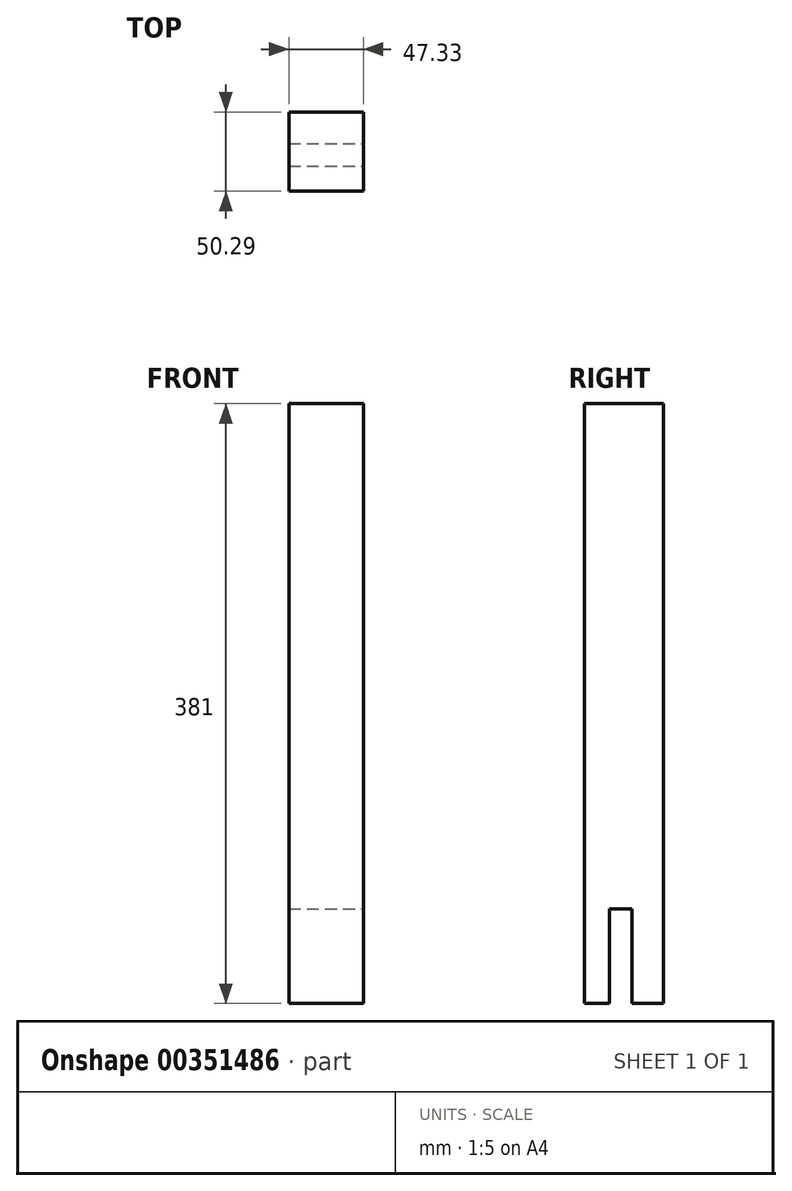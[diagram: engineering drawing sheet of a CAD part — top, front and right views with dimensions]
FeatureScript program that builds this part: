
annotation { "Feature Type Name" : "Feature", "Feature Type Description" : "" }
export const myFeature = defineFeature(function(context is Context, id is Id, definition is map)
    precondition{}
    {
        {
            var Q0;
            Q0=qCreatedBy(makeId("Top.planeOp"),FACE);
            var sketch = newSketch(context, id + "F0", { "sketchPlane" : qUnion([Q0])});
            skLineSegment(sketch, "E0", {"start": v(0, 50.29) * mm, "end": v(47.33, 50.29) * mm});
            skLineSegment(sketch, "E1", {"start": v(47.33, 50.29) * mm, "end": v(47.33, 0) * mm});
            skLineSegment(sketch, "E2", {"start": v(47.33, 0) * mm, "end": v(0, 0) * mm});
            skLineSegment(sketch, "E3", {"start": v(0, 0) * mm, "end": v(0, 50.29) * mm});
            skSolve(sketch);
        }
        {
            var Q0;
            Q0=makeQuery(id+"F0.imprint","IMPRINT",FACE,{"disambiguationData":[TD([[makeQuery(id+"F0.imprint","IMPRINT",EDGE,{"derivedFrom":sQuery(id+"F0.wireOp",EDGE,"E0")}),-1.0]])]});
            extrude(context, id + "F1", {"entities" : qUnion([Q0]), "depth" : 381 * mm});
        }
        {
            var Q0;
            Q0=makeQuery(id+"F1.opExtrude","SWEPT_FACE",FACE,{"disambiguationData":[OSD([sQuery(id+"F0.wireOp",EDGE,"E1")])]});
            var sketch = newSketch(context, id + "F2", { "sketchPlane" : qUnion([Q0])});
            skLineSegment(sketch, "E4.bottom", {"start": v(16.08, 0) * mm, "end": v(30.28, 0) * mm});
            skLineSegment(sketch, "E4.top", {"start": v(16.08, 60.04) * mm, "end": v(30.28, 60.04) * mm});
            skLineSegment(sketch, "E4.left", {"start": v(16.08, 0) * mm, "end": v(16.08, 60.04) * mm});
            skLineSegment(sketch, "E4.right", {"start": v(30.28, 0) * mm, "end": v(30.28, 60.04) * mm});
            skSolve(sketch);
        }
        {
            var Q0;
            Q0=makeQuery(id+"F2.imprint","IMPRINT",FACE,{"disambiguationData":[TD([[makeQuery(id+"F2.imprint","IMPRINT",EDGE,{"derivedFrom":sQuery(id+"F2.wireOp",EDGE,"E4.bottom")}),-1.0]])]});
            var Q1;
            Q1=makeQuery(id+"F1.opExtrude","SWEPT_FACE",FACE,{"disambiguationData":[OSD([sQuery(id+"F0.wireOp",EDGE,"E3")])]});
            extrude(context, id + "F3", {"entities" : qUnion([Q0]), "operationType" : NewBodyOperationType.REMOVE, "endBound" : BoundingType.UP_TO_SURFACE, "oppositeDirection" : true, "endBoundEntityFace" : qUnion([Q1]), "depth" : 25.4 * mm});
        }
    });
